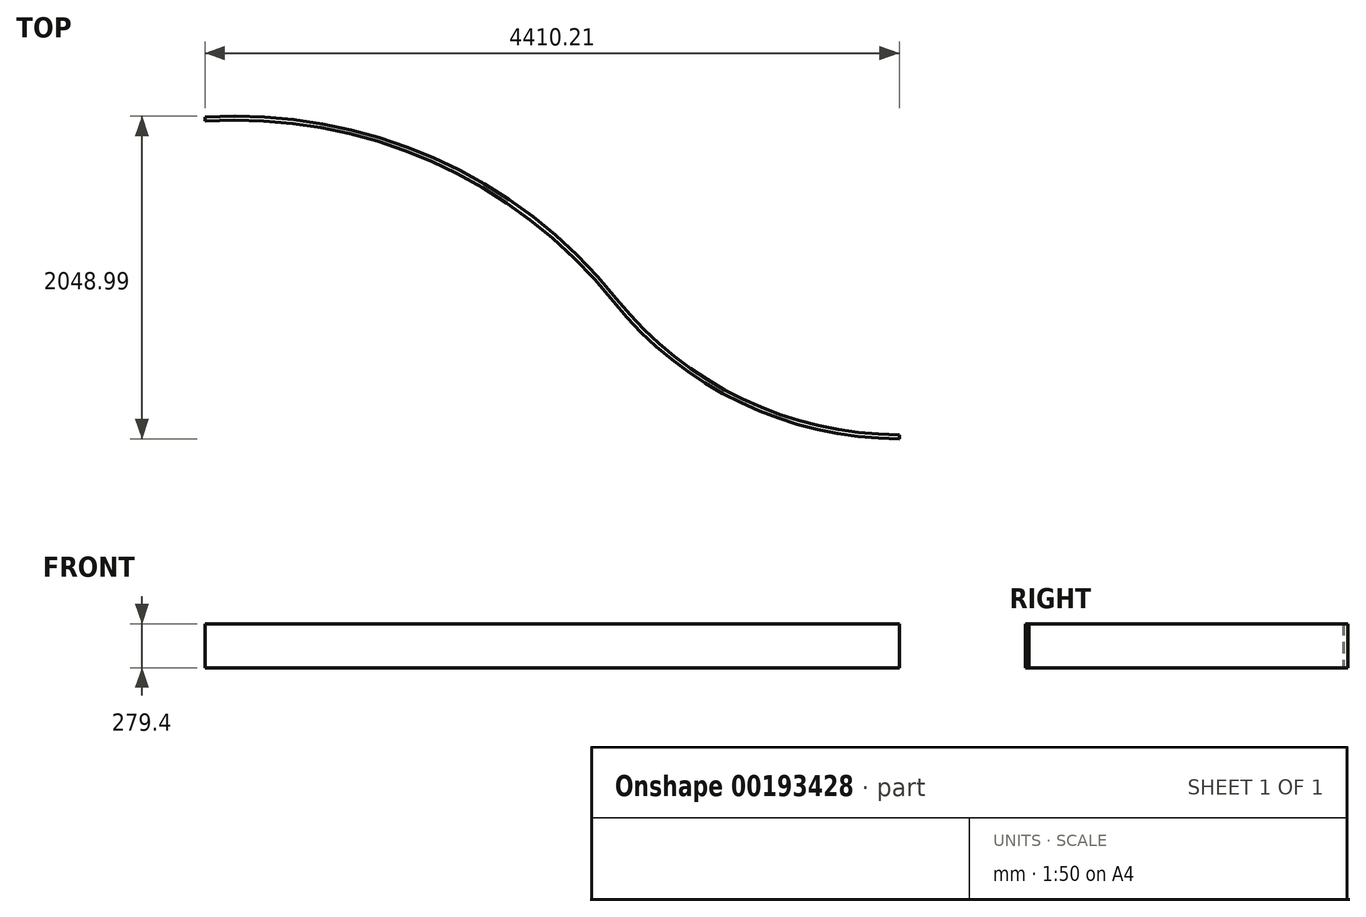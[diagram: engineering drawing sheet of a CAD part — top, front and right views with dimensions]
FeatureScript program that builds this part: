
annotation { "Feature Type Name" : "Feature", "Feature Type Description" : "" }
export const myFeature = defineFeature(function(context is Context, id is Id, definition is map)
    precondition{}
    {
        {
            var Q0;
            Q0=qCreatedBy(makeId("Top.planeOp"),FACE);
            var sketch = newSketch(context, id + "F0", { "sketchPlane" : qUnion([Q0])});
            skLineSegment(sketch, "E0", {"start": v(1858.33, -532.32) * mm, "end": v(1858.33, -1141.92) * mm});
            skArc(sketch, "E1", {"start": v(1858.33, -532.32) * mm, "mid": v(646, -30.15) * mm, "end": v(143.83, 1182.18) * mm});
            skArc(sketch, "E2.0", {"start": v(1858.33, -837.12) * mm, "mid": v(983.7, -637.87) * mm, "end": v(281.67, -79.46) * mm});
            skArc(sketch, "E3.0", {"start": v(1858.33, -1141.92) * mm, "mid": v(851.68, -912.6) * mm, "end": v(43.69, -269.9) * mm});
            skLineSegment(sketch, "E4", {"start": v(-2522.77, 1182.18) * mm, "end": v(-2551.88, 875.2) * mm});
            skPoint(sketch, "E5", {"position": v(-2522.77, 1182.18) * mm});
            skArc(sketch, "E6", {"start": v(281.67, -79.46) * mm, "mid": v(-968.46, 889.45) * mm, "end": v(-2522.77, 1182.18) * mm});
            skArc(sketch, "E7.0", {"start": v(43.69, -269.9) * mm, "mid": v(-1113.85, 620.55) * mm, "end": v(-2551.88, 875.2) * mm});
            skPoint(sketch, "E8.orphan", {"position": v(-2642.4, -79.46) * mm});
            skLineSegment(sketch, "E9", {"start": v(1858.33, 1182.18) * mm, "end": v(-206.1, -882.24) * mm});
            skLineSegment(sketch, "E10", {"start": v(646, -30.15) * mm, "end": v(502.3, 113.53) * mm});
            skLineSegment(sketch, "E11.MirrorCS", {"start": v(646, -30.15) * mm, "end": v(789.68, -173.84) * mm});
            skLineSegment(sketch, "E12", {"start": v(-2549.46, 900.81) * mm, "end": v(-2522.77, 1182.18) * mm});
            skLineSegment(sketch, "E13.bottom", {"start": v(1832.93, -532.13) * mm, "end": v(1858.33, -532.13) * mm});
            skLineSegment(sketch, "E13.top", {"start": v(1832.93, -532.32) * mm, "end": v(1858.33, -532.32) * mm});
            skLineSegment(sketch, "E13.left", {"start": v(1832.93, -532.13) * mm, "end": v(1832.93, -532.32) * mm});
            skLineSegment(sketch, "E13.right", {"start": v(1858.33, -532.13) * mm, "end": v(1858.33, -532.32) * mm});
            skLineSegment(sketch, "E14", {"start": v(502.3, 113.53) * mm, "end": v(125.14, -263.64) * mm});
            skLineSegment(sketch, "E15", {"start": v(125.14, -263.64) * mm, "end": v(412.5, -551) * mm});
            skLineSegment(sketch, "E16.trimOffspring", {"start": v(412.5, -551) * mm, "end": v(789.68, -173.84) * mm});
            skArc(sketch, "E17.0", {"start": v(63.52, -254.02) * mm, "mid": v(-1101.73, 642.97) * mm, "end": v(-2549.46, 900.81) * mm});
            skArc(sketch, "E18.0", {"start": v(1858.33, -1116.52) * mm, "mid": v(862.68, -889.7) * mm, "end": v(63.52, -254.02) * mm});
            skSolve(sketch);
        }
        {
            var Q0;
            {var subQ7=sQuery(id+"F0.wireOp",EDGE,"E4");Q0=makeQuery(id+"F0.imprint","IMPRINT",FACE,{"disambiguationData":[TD([[makeQuery(id+"F0.imprint","IMPRINT",EDGE,{"derivedFrom":subQ7}),1.0]])]});}
            var Q1;
            {var subQ0=sQuery(id+"F0.wireOp",EDGE,"E3.0");var subQ1=sQuery(id+"F0.wireOp",EDGE,"E0");var subQ2=makeQuery(id+"F0.imprint","INTERSECT",VERTEX,{"derivedFrom":[subQ1,subQ0]});Q1=makeQuery(id+"F0.imprint","IMPRINT",FACE,{"disambiguationData":[TD([[makeQuery(id+"F0.imprint","IMPRINT",EDGE,{"disambiguationData":[TD([[subQ2,1.0]])],"derivedFrom":subQ1}),-1.0]])]});}
            extrude(context, id + "F1", {"entities" : qUnion([Q0, Q1]), "depth" : 279.4 * mm});
        }
    });
